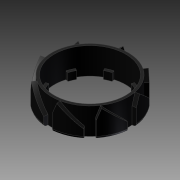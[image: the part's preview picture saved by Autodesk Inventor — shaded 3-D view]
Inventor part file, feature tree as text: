
AUTODESK INVENTOR PART (.ipt)
format: ipt  version: 2012 (Build 160160000, 160)  size: 298,496 bytes
history: native  units: mm
features: sketch x5, extrude x3, pattern_circular x3, helix x2, fillet x1, mirror x1
ambient origin geometry x8: Origin, YZ Plane, XZ Plane, XY Plane, X Axis, Y Axis, Z Axis, Center Point
bodies: Solid1 (feature_tree)
feature tree (15):
  sketch  "Sketch1"  dims[d0=64.0mm d1=54.2mm d2=50.0mm]
  extrude  "Extrusion2"  Depth=54.2mm
  sketch  "Sketch3"  dims[d3=58.0mm d6=20.0mm d7=0.0mm]
  fillet  "Fillet3"  Radius=50.0mm
  sketch  "Sketch5"  dims[d10=4.0mm]
  extrude  "Extrusion9"  Depth=20.0mm TaperAngle=0.0deg
  pattern_circular  "Circular Pattern6"  [2 undecoded]
  sketch  "Sketch7"  dims[d17=2.0mm]
  helix  "Coil5"  [1 undecoded]
  helix  "Coil6"  [1 undecoded]
  pattern_circular  "Circular Pattern7"  [2 undecoded]
  extrude  "Extrusion11"  Depth=10.0mm TaperAngle=0.0deg
  mirror  "Mirror5"
  pattern_circular  "Circular Pattern8"  Count=8 Angle=360.0deg
  sketch  "Sketch9"  dims[d35=40.1mm d36=49.0mm d37=1.012291mm d46=2.0mm d47=4.0mm d58=4.0mm d59=26.0mm d86=2.094395mm d87=10.0mm d88=0.0mm d89=80.0mm d90=360.0deg d92=1.047198mm d93=29.0mm d94=22.0mm d95=10.0mm d96=16.0mm d97=0.9375mm d98=0.0mm d99=90.0deg d100=90.0deg d101=0.0mm d102=0.0mm d103=16.0mm d104=10.0mm d105=16.0mm d106=0.3125mm d107=0.0mm d108=90.0deg d109=90.0deg d110=0.0mm d111=0.0mm d112=80.0mm d113=360.0deg d115=18.0mm d127=1.012291mm d128=22.5deg d129=50.1mm d130=55.0mm d131=5.8mm d132=0.0mm d133=80.0mm d134=360.0deg]
note: 6 required parameter values undecoded (feature->parameter linkage not recoverable at this tier; creation-order binding heuristic only, values carry confidence <= 0.55)
